# Revit family: 18274 Качели парковые «Белек» Хоббика
name_source: partatom
category: Антураж
revit_build: Autodesk Revit 2018 (Build: 20180423_1000(x64)
units: mm (PartAtom-declared; Revit-internal decimal feet)

## family parameters
Всегда вертикально = Да
Источник визуального образа = Геометрия семейства
На основе рабочей плоскости = Нет
Общий = Нет
При загрузке вырезать с полостями = Нет
Точка расчета площади = Нет

## types (2) — shared parameters
URL = https://hobbyka.ru
Артикул товара = Арт. 18274
Высота = 3000 мм
Группа модели = Парковые качели
Длина = 3000 мм
Изготовитель = ООО «Хоббика»
Изображение типоразмера = Качели парковые «Белек» Арт 18274.jpg
Материал изделия = Сталь, дерево
Цвет каркаса = Сталь
Ширина = 710 мм

## per-type parameters (varying)
| type | Ангарская сосна | Лиственница | Описание | Цвет отделки |
| Версия Ангарская сосна | Да | Нет | Качели парковые «Белек». Версия Ангарская сосна | Ангарская сосна |
| Версия Лиственница | Нет | Да | Качели парковые «Белек». Версия Лиственница | Лиственница |
